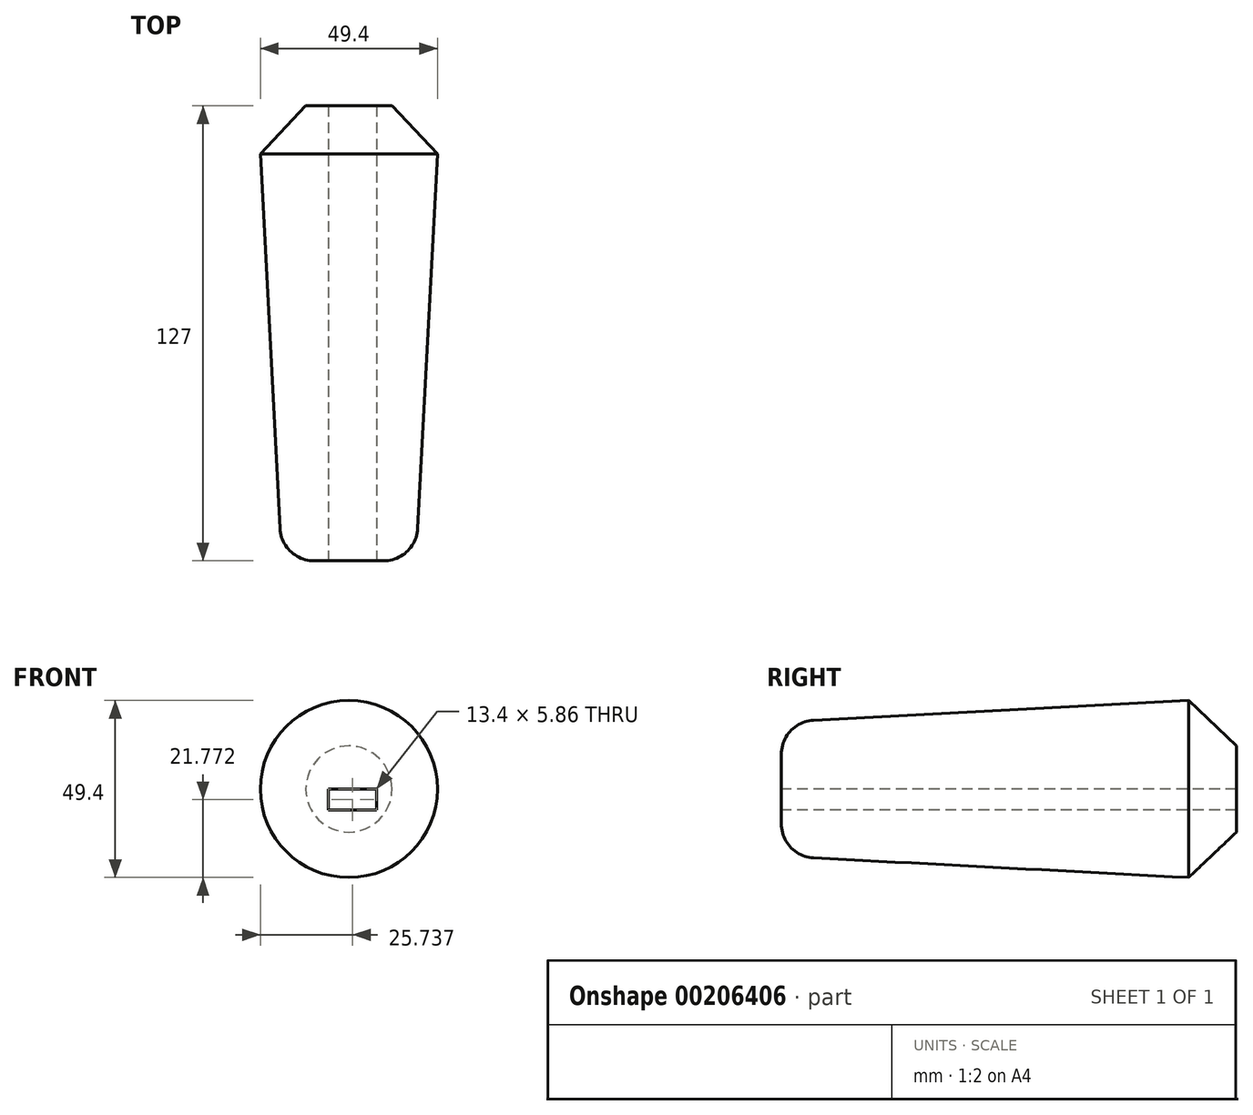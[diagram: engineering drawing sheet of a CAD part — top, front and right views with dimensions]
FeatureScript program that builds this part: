
annotation { "Feature Type Name" : "Feature", "Feature Type Description" : "" }
export const myFeature = defineFeature(function(context is Context, id is Id, definition is map)
    precondition{}
    {
        {
            var Q0;
            Q0=qCreatedBy(makeId("Front.planeOp"),FACE);
            var sketch = newSketch(context, id + "F0", { "sketchPlane" : qUnion([Q0])});
            skCircle(sketch, "E0", {"center": v(0, 0) * mm, "radius": 25.4 * mm});
            skSolve(sketch);
        }
        {
            var Q0;
            Q0=makeQuery(id+"F0.imprint","IMPRINT",FACE,{"disambiguationData":[TD([[makeQuery(id+"F0.imprint","IMPRINT",EDGE,{"derivedFrom":sQuery(id+"F0.wireOp",EDGE,"E0")}),1.0]])]});
            extrude(context, id + "F1", {"entities" : qUnion([Q0]), "depth" : 127 * mm, "hasDraft" : true, "draftAngle" : 3 * degree, "draftPullDirection" : true});
        }
        {
            var Q0;
            Q0=makeQuery(id+"F1.opExtrude","CAP_FACE",FACE,{"disambiguationData":[OSD([sQuery(id+"F0.wireOp",EDGE,"E0")])],"isStart":false});
            fillet(context, id + "F2", {"entities" : qUnion([Q0]), "radius" : 9.52 * mm, "tangentPropagation" : true, "allowEdgeOverflow" : false});
        }
        {
            var Q0;
            Q0=makeQuery(id+"F1.opExtrude","CAP_EDGE",EDGE,{"disambiguationData":[OSD([sQuery(id+"F0.wireOp",EDGE,"E0")])],"isStart":true});
            chamfer(context, id + "F3", {"entities" : qUnion([Q0]), "width" : 12.7 * mm, "tangentPropagation" : true});
        }
        {
            var Q0;
            Q0=makeQuery(id+"F1.opExtrude","CAP_FACE",FACE,{"disambiguationData":[OSD([sQuery(id+"F0.wireOp",EDGE,"E0")])],"isStart":false});
            var sketch = newSketch(context, id + "F4", { "sketchPlane" : qUnion([Q0])});
            skLineSegment(sketch, "E1.bottom", {"start": v(-5.67, 0) * mm, "end": v(7.74, 0) * mm});
            skLineSegment(sketch, "E1.top", {"start": v(-5.67, -5.86) * mm, "end": v(7.74, -5.86) * mm});
            skLineSegment(sketch, "E1.left", {"start": v(-5.67, 0) * mm, "end": v(-5.67, -5.86) * mm});
            skLineSegment(sketch, "E1.right", {"start": v(7.74, 0) * mm, "end": v(7.74, -5.86) * mm});
            skSolve(sketch);
        }
        {
            var Q0;
            Q0=makeQuery(id+"F4.imprint","IMPRINT",FACE,{"disambiguationData":[TD([[makeQuery(id+"F4.imprint","IMPRINT",EDGE,{"derivedFrom":sQuery(id+"F4.wireOp",EDGE,"E1.bottom")}),-1.0]])]});
            extrude(context, id + "F5", {"entities" : qUnion([Q0]), "operationType" : NewBodyOperationType.REMOVE, "endBound" : BoundingType.THROUGH_ALL, "oppositeDirection" : true, "depth" : 127 * mm});
        }
    });
